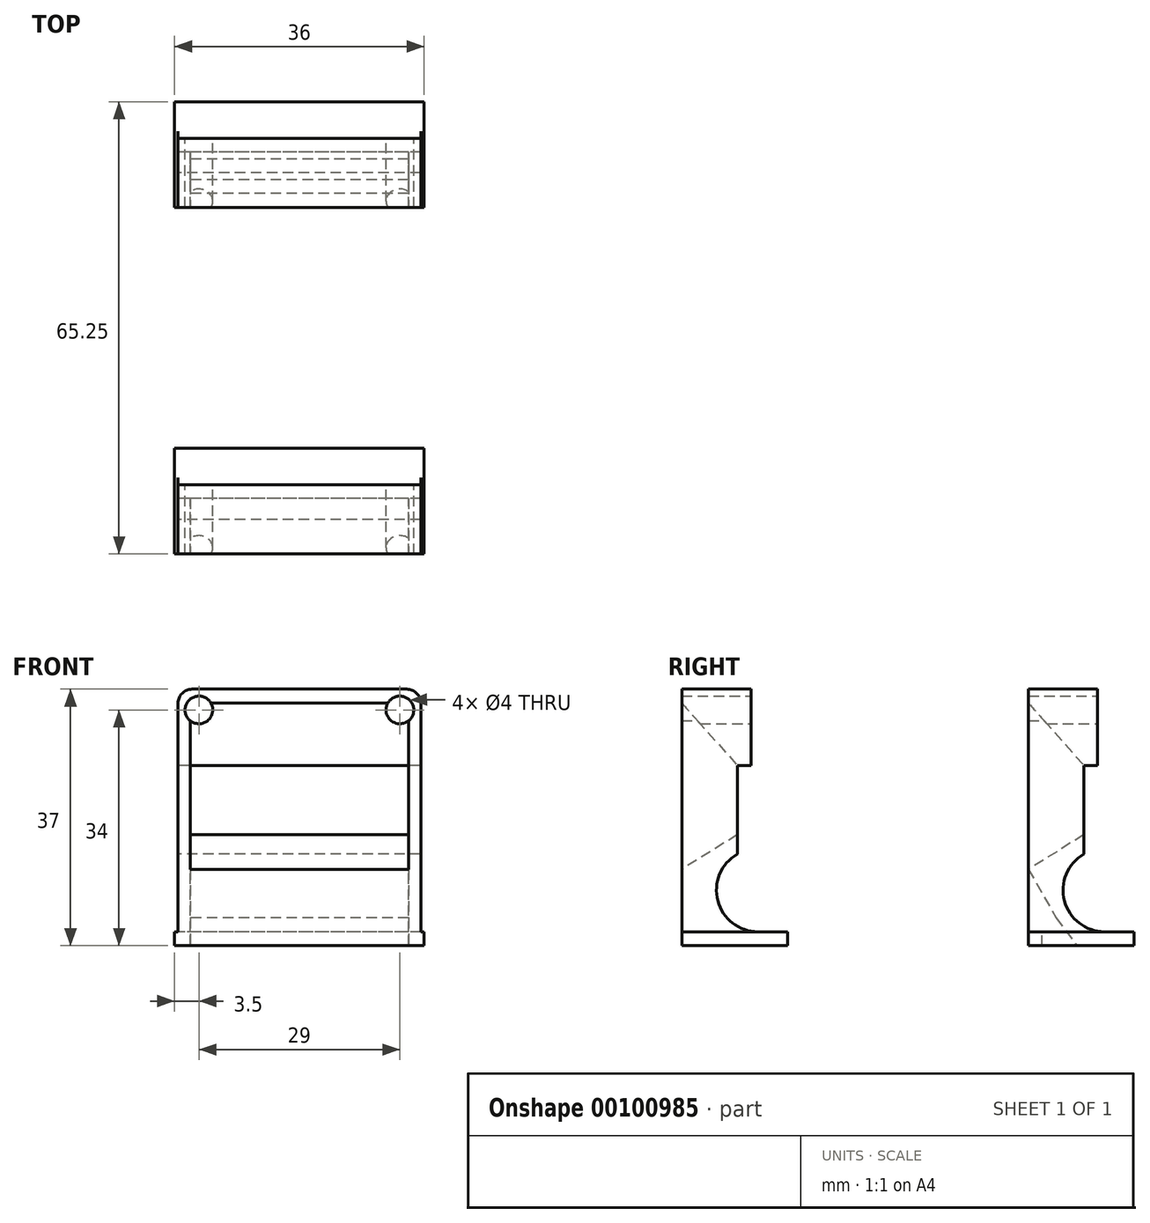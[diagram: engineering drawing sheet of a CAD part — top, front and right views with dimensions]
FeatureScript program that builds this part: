
annotation { "Feature Type Name" : "Feature", "Feature Type Description" : "" }
export const myFeature = defineFeature(function(context is Context, id is Id, definition is map)
    precondition{}
    {
        {
            var Q0;
            Q0=qCreatedBy(makeId("Right.planeOp"),FACE);
            var sketch = newSketch(context, id + "F0", { "sketchPlane" : qUnion([Q0])});
            skLineSegment(sketch, "E0", {"start": v(0, 0) * mm, "end": v(0, 37) * mm});
            skLineSegment(sketch, "E1", {"start": v(0, 37) * mm, "end": v(10, 37) * mm});
            skLineSegment(sketch, "E2", {"start": v(10, 37) * mm, "end": v(10, 26) * mm});
            skLineSegment(sketch, "E3", {"start": v(10, 26) * mm, "end": v(8, 26) * mm});
            skLineSegment(sketch, "E4", {"start": v(8, 26) * mm, "end": v(8, 13.2) * mm});
            skLineSegment(sketch, "E5", {"start": v(0, 0) * mm, "end": v(15.25, 0) * mm});
            skLineSegment(sketch, "E6", {"start": v(15.25, 0) * mm, "end": v(15.25, 2) * mm});
            skLineSegment(sketch, "E7", {"start": v(0, 2) * mm, "end": v(11, 2) * mm, "construction": true});
            skLineSegment(sketch, "E8", {"start": v(11, 2) * mm, "end": v(11, 14) * mm, "construction": true});
            skArc(sketch, "E9", {"start": v(8, 13.2) * mm, "mid": v(5.2, 6.45) * mm, "end": v(11, 2) * mm});
            skLineSegment(sketch, "E10", {"start": v(15.25, 2) * mm, "end": v(11, 2) * mm});
            skPoint(sketch, "E11.orphan", {"position": v(8, 14) * mm});
            skSolve(sketch);
        }
        {
            var Q0;
            Q0 = qSketchRegion(id + "F0", true);
            extrude(context, id + "F1", {"entities" : qUnion([Q0]), "depth" : 35 * mm});
        }
        {
            var Q0;
            Q0=makeQuery(id+"F1.opExtrude","SWEPT_FACE",FACE,{"disambiguationData":[OSD([sQuery(id+"F0.wireOp",EDGE,"E2")])]});
            var sketch = newSketch(context, id + "F2", { "sketchPlane" : qUnion([Q0])});
            skCircle(sketch, "E12", {"center": v(-32, 34) * mm, "radius": 2 * mm});
            skLineSegment(sketch, "E13", {"start": v(-17.5, 37) * mm, "end": v(-17.5, 0) * mm, "construction": true});
            skPoint(sketch, "E13.endSnap0", {"position": v(-17.5, 26) * mm});
            skCircle(sketch, "E14.MirrorC", {"center": v(-3, 34) * mm, "radius": 2 * mm});
            skSolve(sketch);
        }
        {
            var Q0;
            Q0 = qSketchRegion(id + "F2", true);
            var Q1;
            Q1=makeQuery(id+"F1.opExtrude","SWEPT_FACE",FACE,{"disambiguationData":[OSD([sQuery(id+"F0.wireOp",EDGE,"E0")])]});
            extrude(context, id + "F3", {"entities" : qUnion([Q0]), "operationType" : NewBodyOperationType.REMOVE, "endBound" : BoundingType.UP_TO_SURFACE, "oppositeDirection" : true, "endBoundEntityFace" : qUnion([Q1]), "depth" : 25 * mm});
        }
        {
            var Q0;
            Q0=makeQuery(id+"F1.opExtrude","CAP_EDGE",EDGE,{"disambiguationData":[OSD([sQuery(id+"F0.wireOp",EDGE,"E1")])],"isStart":true});
            var Q1;
            Q1=makeQuery(id+"F1.opExtrude","CAP_EDGE",EDGE,{"disambiguationData":[OSD([sQuery(id+"F0.wireOp",EDGE,"E1")])],"isStart":false});
            fillet(context, id + "F4", {"entities" : qUnion([Q0, Q1]), "radius" : 2 * mm, "tangentPropagation" : true, "allowEdgeOverflow" : false});
        }
        {
            var Q0;
            Q0=qCreatedBy(makeId("Right.planeOp"),FACE);
            cPlane(context, id + "F5", {"entities" : qUnion([Q0]), "cplaneType" : CPlaneType.OFFSET, "offset" : 17.5 * mm, "width" : 150 * mm, "height" : 150 * mm});
        }
        {
            var Q0;
            Q0=qCreatedBy(id+"F5.planeOp",FACE);
            var sketch = newSketch(context, id + "F6", { "sketchPlane" : qUnion([Q0])});
            skLineSegment(sketch, "E15", {"start": v(0, 0) * mm, "end": v(0, 37) * mm, "construction": true});
            skLineSegment(sketch, "E16", {"start": v(0, 37) * mm, "end": v(10, 37) * mm, "construction": true});
            skLineSegment(sketch, "E17.0", {"start": v(0, 35) * mm, "end": v(10, 35) * mm, "construction": true});
            skLineSegment(sketch, "E18", {"start": v(10, 37) * mm, "end": v(10, 26) * mm, "construction": true});
            skLineSegment(sketch, "E19", {"start": v(10, 26) * mm, "end": v(8, 26) * mm, "construction": true});
            skLineSegment(sketch, "E20", {"start": v(0, 35) * mm, "end": v(8, 26) * mm});
            skLineSegment(sketch, "E21", {"start": v(8, 26) * mm, "end": v(8, 16) * mm});
            skLineSegment(sketch, "E22.0", {"start": v(0, 11) * mm, "end": v(10, 11) * mm, "construction": true});
            skLineSegment(sketch, "E23", {"start": v(8, 16) * mm, "end": v(0, 11) * mm});
            skLineSegment(sketch, "E24.0", {"start": v(0, 4) * mm, "end": v(10, 4) * mm, "construction": true});
            skLineSegment(sketch, "E25.0", {"start": v(4, 0) * mm, "end": v(4, 37) * mm, "construction": true});
            skLineSegment(sketch, "E26", {"start": v(0, 11) * mm, "end": v(4, 4) * mm});
            skLineSegment(sketch, "E27", {"start": v(0, 0) * mm, "end": v(7, 0) * mm, "construction": true});
            skLineSegment(sketch, "E28", {"start": v(4, 4) * mm, "end": v(7, 0) * mm});
            skLineSegment(sketch, "E29.top", {"start": v(0, 2) * mm, "end": v(2, 2) * mm});
            skLineSegment(sketch, "E29.right", {"start": v(2, 0) * mm, "end": v(2, 2) * mm});
            skLineSegment(sketch, "E30", {"start": v(7, 0) * mm, "end": v(2, 0) * mm});
            skLineSegment(sketch, "E31", {"start": v(0, 2) * mm, "end": v(0, 11) * mm});
            skLineSegment(sketch, "E32", {"start": v(0, 11) * mm, "end": v(0, 35) * mm});
            skSolve(sketch);
        }
        {
            var Q0;
            Q0 = qSketchRegion(id + "F6", true);
            extrude(context, id + "F7", {"entities" : qUnion([Q0]), "operationType" : NewBodyOperationType.REMOVE, "depth" : 15.75 * mm, "hasSecondDirection" : true, "secondDirectionOppositeDirection" : true, "secondDirectionDepth" : 15.75 * mm});
        }
        {
            var Q0;
            Q0=makeQuery(id+"F1.opExtrude","SWEPT_FACE",FACE,{"disambiguationData":[OSD([sQuery(id+"F0.wireOp",EDGE,"E5")])]});
            var sketch = newSketch(context, id + "F8", { "sketchPlane" : qUnion([Q0])});
            skLineSegment(sketch, "E33", {"start": v(17.5, 0) * mm, "end": v(17.5, -15.25) * mm, "construction": true});
            skLineSegment(sketch, "E34.0", {"start": v(-0.5, 0) * mm, "end": v(-0.5, -15.25) * mm});
            skLineSegment(sketch, "E35.0", {"start": v(35.5, 0) * mm, "end": v(35.5, -15.25) * mm});
            skLineSegment(sketch, "E36", {"start": v(-0.5, 0) * mm, "end": v(35.5, 0) * mm});
            skLineSegment(sketch, "E37", {"start": v(-0.5, -15.25) * mm, "end": v(35.5, -15.25) * mm});
            skLineSegment(sketch, "E38.0", {"start": v(1.75, -7) * mm, "end": v(1.75, -2) * mm});
            skLineSegment(sketch, "E38.1", {"start": v(33.25, -2) * mm, "end": v(1.75, -2) * mm});
            skLineSegment(sketch, "E38.2", {"start": v(33.25, -7) * mm, "end": v(33.25, -2) * mm});
            skLineSegment(sketch, "E38.3", {"start": v(33.25, -7) * mm, "end": v(1.75, -7) * mm});
            skSolve(sketch);
        }
        {
            var Q0;
            Q0 = qSketchRegion(id + "F8", true);
            extrude(context, id + "F9", {"entities" : qUnion([Q0]), "operationType" : NewBodyOperationType.ADD, "oppositeDirection" : true, "depth" : 2 * mm});
        }
        {
            var Q0;
            Q0=makeQuery(id+"F1.opExtrude","SWEPT_BODY",BODY,{"disambiguationData":[OSD([sQuery(id+"F0.wireOp",EDGE,"E0"),sQuery(id+"F0.wireOp",EDGE,"E1"),sQuery(id+"F0.wireOp",EDGE,"E2"),sQuery(id+"F0.wireOp",EDGE,"E3"),sQuery(id+"F0.wireOp",EDGE,"E4"),sQuery(id+"F0.wireOp",EDGE,"E5"),sQuery(id+"F0.wireOp",EDGE,"E6"),sQuery(id+"F0.wireOp",EDGE,"E9"),sQuery(id+"F0.wireOp",EDGE,"E10")])]});
            transform(context, id + "F10", {"entities" : qUnion([Q0]), "transformType" : TransformType.TRANSLATION_3D, "dx" : 0 * mm, "dy" : -50 * mm, "dz" : 0 * mm, "makeCopy" : true});
        }
        {
            var Q0;
            Q0=makeQuery(id+"F10.opPattern","COPY",FACE,{"derivedFrom":makeQuery(id+"F7.boolean.opBoolean","COPY",FACE,{"derivedFrom":makeQuery(id+"F7.opExtrude","CAP_FACE",FACE,{"disambiguationData":[OSD([sQuery(id+"F6.wireOp",EDGE,"E26"),sQuery(id+"F6.wireOp",EDGE,"E28"),sQuery(id+"F6.wireOp",EDGE,"E29.top"),sQuery(id+"F6.wireOp",EDGE,"E29.right"),sQuery(id+"F6.wireOp",EDGE,"E30"),sQuery(id+"F6.wireOp",EDGE,"E31")])],"isStart":false})}),"instanceName":"1"});
            var sketch = newSketch(context, id + "F11", { "sketchPlane" : qUnion([Q0])});
            skSolve(sketch);
        }
        {
            var Q0;
            Q0=makeQuery(id+"F11.imprint","IMPRINT",FACE,{"disambiguationData":[TD([[makeQuery(id+"F11.imprint","IMPRINT",EDGE,{"derivedFrom":makeQuery(id+"F10.opPattern","COPY",EDGE,{"derivedFrom":makeQuery(id+"F7.boolean.opBoolean","COPY",EDGE,{"derivedFrom":makeQuery(id+"F7.opExtrude","CAP_EDGE",EDGE,{"disambiguationData":[OSD([sQuery(id+"F6.wireOp",EDGE,"E26")])],"isStart":false})}),"instanceName":"1"})}),1.0]])]});
            var Q1;
            Q1=makeQuery(id+"F10.opPattern","COPY",FACE,{"derivedFrom":makeQuery(id+"F7.boolean.opBoolean","COPY",FACE,{"derivedFrom":makeQuery(id+"F7.opExtrude","CAP_FACE",FACE,{"disambiguationData":[OSD([sQuery(id+"F6.wireOp",EDGE,"E26"),sQuery(id+"F6.wireOp",EDGE,"E28"),sQuery(id+"F6.wireOp",EDGE,"E29.top"),sQuery(id+"F6.wireOp",EDGE,"E29.right"),sQuery(id+"F6.wireOp",EDGE,"E30"),sQuery(id+"F6.wireOp",EDGE,"E31")])],"isStart":true})}),"instanceName":"1"});
            extrude(context, id + "F12", {"entities" : qUnion([Q0]), "operationType" : NewBodyOperationType.ADD, "endBound" : BoundingType.UP_TO_SURFACE, "endBoundEntityFace" : qUnion([Q1]), "depth" : 25 * mm});
        }
    });
